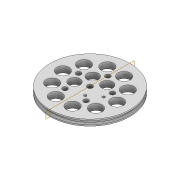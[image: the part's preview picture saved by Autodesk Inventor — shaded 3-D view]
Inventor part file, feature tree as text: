
AUTODESK INVENTOR PART (.ipt)
format: ipt  version: 2022 (Build 260153000, 153)  size: 376,832 bytes
history: native  units: mm
features: extrude x7, sketch x6, plane x3, projected_geometry x2, pattern_circular x1, fillet x1, mirror x1
ambient origin geometry x8: Origin, YZ Plane, XZ Plane, XY Plane, X Axis, Y Axis, Z Axis, Center Point
bodies: Solid1 (feature_tree)
feature tree (21):
  extrude  "Extrusion1"  Depth=60.0mm
  extrude  "Extrusion2"  Depth=3.0mm TaperAngle=0.0deg
  pattern_circular  "Circular Pattern1"  Count=5 Angle=360.0deg
  plane  "Work Plane1"
  plane  "Work Plane2"
  extrude  "Extrusion3"  [1 undecoded]
  extrude  "Extrusion4"  Depth=5.0mm
  fillet  "Fillet1"  Radius=1.5mm
  plane  "Work Plane3"
  extrude  "Extrusion9"  Depth=5.0mm
  mirror  "Mirror1"
  sketch  "Sketch9"  dims[d13=9.599311mm d14=-9.599311mm d15=1.5mm d16=1.5mm d17=1.7mm d18=10.0mm d19=0.0mm d20=1.5mm d21=1.5mm d22=1.7mm d23=10.0mm d24=0.0mm d25=1.0mm d46=22.0mm d47=3.141593mm d48=22.0mm d49=10.0mm d50=10.0mm d51=4.0mm d52=14.5mm d53=6.283185mm d54=4.0mm d55=14.5mm d56=65.0mm d57=1.0mm d58=0.0mm d59=2.1mm d60=2.1mm d61=4.5mm d62=8.4mm d63=1.9mm d64=13.0mm d65=5.0mm d66=0.0mm d67=100.0mm d68=0.0mm]
  extrude  "Extrusion10"  Depth=10.0mm TaperAngle=0.0deg
  extrude  "Extrusion11"  Depth=5.0mm
  sketch  "Sketch1"  dims[d0=4.2mm d2=60.0mm]
  sketch  "Sketch2"  dims[d3=4.0mm d4=3.0mm d5=0.0mm]
  sketch  "Sketch3"  dims[d6=9.0mm]
  sketch  "Sketch4"  dims[d7=10.0mm]
  sketch  "Sketch8"  dims[d8=10.0mm d9=0.0mm d10=50.0mm d11=360.0deg]
  projected_geometry  "Projected Loop3"
  projected_geometry  "Projected Loop4"
note: 1 required parameter value undecoded (feature->parameter linkage not recoverable at this tier; creation-order binding heuristic only, values carry confidence <= 0.55)
